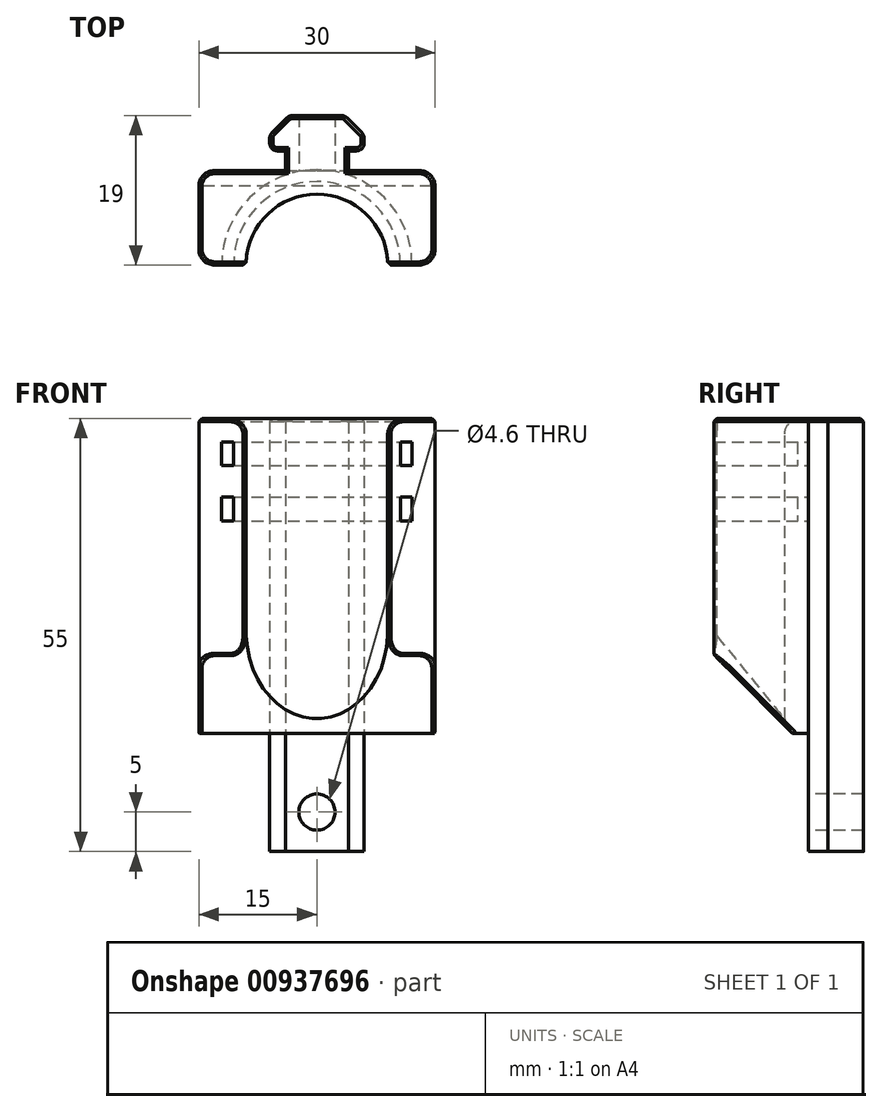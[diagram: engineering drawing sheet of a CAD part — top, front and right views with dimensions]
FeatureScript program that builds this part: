
annotation { "Feature Type Name" : "Feature", "Feature Type Description" : "" }
export const myFeature = defineFeature(function(context is Context, id is Id, definition is map)
    precondition{}
    {
        {
            var Q0;
            Q0=qCreatedBy(makeId("Front.planeOp"),FACE);
            var sketch = newSketch(context, id + "F0", { "sketchPlane" : qUnion([Q0])});
            skLineSegment(sketch, "E0.bottom", {"start": v(-15, 40) * mm, "end": v(15, 40) * mm});
            skLineSegment(sketch, "E0.top", {"start": v(-15, 0) * mm, "end": v(15, 0) * mm});
            skLineSegment(sketch, "E0.left", {"start": v(-15, 40) * mm, "end": v(-15, 0) * mm});
            skLineSegment(sketch, "E0.right", {"start": v(15, 40) * mm, "end": v(15, 0) * mm});
            skSolve(sketch);
        }
        {
            var Q0;
            Q0=makeQuery(id+"F0.imprint","IMPRINT",FACE,{"disambiguationData":[TD([[makeQuery(id+"F0.imprint","IMPRINT",EDGE,{"derivedFrom":sQuery(id+"F0.wireOp",EDGE,"E0.bottom")}),-1.0]])]});
            extrude(context, id + "F1", {"entities" : qUnion([Q0]), "depth" : 3 * mm, "offsetDistance" : 25 * mm});
        }
        {
            var Q0;
            Q0=qCreatedBy(makeId("Top.planeOp"),FACE);
            var sketch = newSketch(context, id + "F2", { "sketchPlane" : qUnion([Q0])});
            skLineSegment(sketch, "E1", {"start": v(-4, 0) * mm, "end": v(-4, 2.5) * mm});
            skLineSegment(sketch, "E2", {"start": v(-4, 2.5) * mm, "end": v(-6, 2.5) * mm});
            skLineSegment(sketch, "E3", {"start": v(-6, 2.5) * mm, "end": v(-6, 4.5) * mm});
            skLineSegment(sketch, "E4", {"start": v(-6, 4.5) * mm, "end": v(-3.5, 7) * mm});
            skLineSegment(sketch, "E5", {"start": v(-3.5, 7) * mm, "end": v(3.5, 7) * mm});
            skLineSegment(sketch, "E6", {"start": v(3.5, 7) * mm, "end": v(6, 4.5) * mm});
            skLineSegment(sketch, "E7", {"start": v(6, 4.5) * mm, "end": v(6, 2.5) * mm});
            skLineSegment(sketch, "E8", {"start": v(6, 2.5) * mm, "end": v(4, 2.5) * mm});
            skLineSegment(sketch, "E9", {"start": v(4, 2.5) * mm, "end": v(4, 0) * mm});
            skLineSegment(sketch, "E10", {"start": v(-4, 0) * mm, "end": v(4, 0) * mm});
            skSolve(sketch);
        }
        {
            var Q0;
            Q0=makeQuery(id+"F2.imprint","IMPRINT",FACE,{"disambiguationData":[TD([[makeQuery(id+"F2.imprint","IMPRINT",EDGE,{"derivedFrom":sQuery(id+"F2.wireOp",EDGE,"E1")}),-1.0]])]});
            var Q1;
            Q1=makeQuery(id+"F1.opExtrude","SWEPT_FACE",FACE,{"disambiguationData":[OSD([sQuery(id+"F0.wireOp",EDGE,"E0.bottom")])]});
            extrude(context, id + "F3", {"entities" : qUnion([Q0]), "operationType" : NewBodyOperationType.ADD, "endBound" : BoundingType.UP_TO_SURFACE, "depth" : 25 * mm, "endBoundEntityFace" : qUnion([Q1]), "offsetDistance" : 25 * mm, "hasSecondDirection" : true, "secondDirectionOppositeDirection" : true, "secondDirectionDepth" : 15 * mm});
        }
        {
            var Q0;
            Q0=makeQuery(id+"F3.boolean.opBoolean","MERGE",FACE,{"derivedFrom":[makeQuery(id+"F1.opExtrude","SWEPT_FACE",FACE,{"disambiguationData":[OSD([sQuery(id+"F0.wireOp",EDGE,"E0.bottom")])]}),makeQuery(id+"F3.opExtrude","CAP_FACE",FACE,{"disambiguationData":[OSD([sQuery(id+"F2.wireOp",EDGE,"E1"),sQuery(id+"F2.wireOp",EDGE,"E2"),sQuery(id+"F2.wireOp",EDGE,"E3"),sQuery(id+"F2.wireOp",EDGE,"E4"),sQuery(id+"F2.wireOp",EDGE,"E5"),sQuery(id+"F2.wireOp",EDGE,"E6"),sQuery(id+"F2.wireOp",EDGE,"E7"),sQuery(id+"F2.wireOp",EDGE,"E8"),sQuery(id+"F2.wireOp",EDGE,"E9"),sQuery(id+"F2.wireOp",EDGE,"E10")])],"isStart":false})]});
            var sketch = newSketch(context, id + "F4", { "sketchPlane" : qUnion([Q0])});
            skCircle(sketch, "E11", {"center": v(0, -12) * mm, "radius": 9 * mm});
            skLineSegment(sketch, "E12", {"start": v(-15, -3) * mm, "end": v(-15, -12) * mm});
            skLineSegment(sketch, "E13", {"start": v(-15, -12) * mm, "end": v(15, -12) * mm});
            skLineSegment(sketch, "E14", {"start": v(15, -12) * mm, "end": v(15, -3) * mm});
            skSolve(sketch);
        }
        {
            var Q0;
            {var subQ6=sQuery(id+"F4.wireOp",EDGE,"E12");Q0=makeQuery(id+"F4.imprint","IMPRINT",FACE,{"disambiguationData":[TD([[makeQuery(id+"F4.imprint","IMPRINT",EDGE,{"derivedFrom":subQ6}),1.0]])]});}
            var Q1;
            {var subQ6=sQuery(id+"F4.wireOp",EDGE,"E14");Q1=makeQuery(id+"F4.imprint","IMPRINT",FACE,{"disambiguationData":[TD([[makeQuery(id+"F4.imprint","IMPRINT",EDGE,{"derivedFrom":subQ6}),1.0]])]});}
            var Q2;
            Q2=makeQuery(id+"F1.opExtrude","SWEPT_FACE",FACE,{"disambiguationData":[OSD([sQuery(id+"F0.wireOp",EDGE,"E0.top")])]});
            extrude(context, id + "F5", {"entities" : qUnion([Q0, Q1]), "operationType" : NewBodyOperationType.ADD, "endBound" : BoundingType.UP_TO_SURFACE, "oppositeDirection" : true, "depth" : 25 * mm, "endBoundEntityFace" : qUnion([Q2]), "offsetDistance" : 25 * mm});
        }
        {
            var Q0;
            {var subQ0=sQuery(id+"F4.wireOp",EDGE,"E13");Q0=makeQuery(id+"F5.opExtrude","CAP_EDGE",EDGE,{"disambiguationData":[OSD([subQ0]),TDD([makeQuery(id+"F4.imprint","IMPRINT",EDGE,{"disambiguationData":[TD([[makeQuery(id+"F4.imprint","INTERSECT",VERTEX,{"derivedFrom":[sQuery(id+"F4.wireOp",EDGE,"E12"),subQ0]}),-1.0]])],"derivedFrom":subQ0})])],"isStart":false});}
            var Q1;
            {var subQ0=sQuery(id+"F4.wireOp",EDGE,"E13");Q1=makeQuery(id+"F5.opExtrude","CAP_EDGE",EDGE,{"disambiguationData":[OSD([subQ0]),TDD([makeQuery(id+"F4.imprint","IMPRINT",EDGE,{"disambiguationData":[TD([[makeQuery(id+"F4.imprint","INTERSECT",VERTEX,{"derivedFrom":[subQ0,sQuery(id+"F4.wireOp",EDGE,"E14")]}),1.0]])],"derivedFrom":subQ0})])],"isStart":false});}
            chamfer(context, id + "F6", {"entities" : qUnion([Q0, Q1]), "chamferType" : ChamferType.OFFSET_ANGLE, "width" : 10 * mm, "oppositeDirection" : false, "angle" : 45 * degree, "tangentPropagation" : true});
        }
        {
            var Q0;
            {var subQ0=sQuery(id+"F4.wireOp",EDGE,"E13");Q0=makeQuery(id+"F5.opExtrude","SWEPT_FACE",FACE,{"disambiguationData":[OSD([subQ0]),TDD([makeQuery(id+"F4.imprint","IMPRINT",EDGE,{"disambiguationData":[TD([[makeQuery(id+"F4.imprint","INTERSECT",VERTEX,{"derivedFrom":[sQuery(id+"F4.wireOp",EDGE,"E12"),subQ0]}),-1.0]])],"derivedFrom":subQ0})])]});}
            var sketch = newSketch(context, id + "F7", { "sketchPlane" : qUnion([Q0])});
            skLineSegment(sketch, "E15.bottom", {"start": v(-12.1, 37) * mm, "end": v(-10.6, 37) * mm});
            skLineSegment(sketch, "E15.top", {"start": v(-12.1, 34) * mm, "end": v(-10.6, 34) * mm});
            skLineSegment(sketch, "E15.left", {"start": v(-12.1, 37) * mm, "end": v(-12.1, 34) * mm});
            skLineSegment(sketch, "E15.right", {"start": v(-10.6, 37) * mm, "end": v(-10.6, 34) * mm});
            skLineSegment(sketch, "E16.bottom", {"start": v(-12.1, 30) * mm, "end": v(-10.6, 30) * mm});
            skLineSegment(sketch, "E16.top", {"start": v(-12.1, 27) * mm, "end": v(-10.6, 27) * mm});
            skLineSegment(sketch, "E16.left", {"start": v(-12.1, 30) * mm, "end": v(-12.1, 27) * mm});
            skLineSegment(sketch, "E16.right", {"start": v(-10.6, 30) * mm, "end": v(-10.6, 27) * mm});
            skLineSegment(sketch, "E17", {"start": v(0, 42) * mm, "end": v(0, 22.6) * mm});
            skSolve(sketch);
        }
        {
            var Q0;
            Q0=makeQuery(id+"F7.imprint","IMPRINT",FACE,{"disambiguationData":[TD([[makeQuery(id+"F7.imprint","IMPRINT",EDGE,{"derivedFrom":sQuery(id+"F7.wireOp",EDGE,"E15.bottom")}),-1.0]])]});
            var Q1;
            Q1=makeQuery(id+"F7.imprint","IMPRINT",FACE,{"disambiguationData":[TD([[makeQuery(id+"F7.imprint","IMPRINT",EDGE,{"derivedFrom":sQuery(id+"F7.wireOp",EDGE,"E16.bottom")}),-1.0]])]});
            var Q2;
            Q2=sQuery(id+"F7.wireOp",EDGE,"E17");
            revolve(context, id + "F8", {"operationType" : NewBodyOperationType.REMOVE, "surfaceOperationType" : NewSurfaceOperationType.NEW, "entities" : qUnion([Q0, Q1]), "axis" : qUnion([Q2]), "revolveType" : RevolveType.FULL, "oppositeDirection" : true});
        }
        {
            var Q0;
            Q0=makeQuery(id+"F3.opExtrude","SWEPT_FACE",FACE,{"disambiguationData":[OSD([sQuery(id+"F2.wireOp",EDGE,"E10")])]});
            var sketch = newSketch(context, id + "F9", { "sketchPlane" : qUnion([Q0])});
            skPoint(sketch, "E18", {"position": v(0, -10) * mm});
            skSolve(sketch);
        }
        {
            var Q0;
            Q0=sQuery(id+"F9.wireOp",VERTEX,"E18");
            var Q1;
            Q1=makeQuery(id+"F1.opExtrude","SWEPT_BODY",BODY,{"disambiguationData":[OSD([sQuery(id+"F0.wireOp",EDGE,"E0.bottom"),sQuery(id+"F0.wireOp",EDGE,"E0.top"),sQuery(id+"F0.wireOp",EDGE,"E0.left"),sQuery(id+"F0.wireOp",EDGE,"E0.right")])]});
            hole(context, id + "F10", {"style" : HoleStyle.SIMPLE, "endStyle" : HoleEndStyle.BLIND, "holeDiameter" : 4.6 * mm, "majorDiameter" : 5 * mm, "holeDepth" : 7 * mm, "isTappedThrough" : true, "tappedDepth" : 20 * mm, "tapClearance" : 3, "locations" : qUnion([Q0]), "scope" : qUnion([Q1])});
        }
        {
            var Q0;
            Q0=makeQuery(id+"F5.opExtrude","SWEPT_EDGE",EDGE,{"disambiguationData":[OSD([sQuery(id+"F4.wireOp",EDGE,"E13"),sQuery(id+"F4.wireOp",EDGE,"E14")])]});
            var Q1;
            Q1=makeQuery(id+"F5.opExtrude","SWEPT_EDGE",EDGE,{"disambiguationData":[OSD([sQuery(id+"F4.wireOp",EDGE,"E12"),sQuery(id+"F4.wireOp",EDGE,"E13")])]});
            var Q2;
            Q2=makeQuery(id+"F1.opExtrude","CAP_EDGE",EDGE,{"disambiguationData":[OSD([sQuery(id+"F0.wireOp",EDGE,"E0.right")])],"isStart":true});
            var Q3;
            Q3=makeQuery(id+"F1.opExtrude","CAP_EDGE",EDGE,{"disambiguationData":[OSD([sQuery(id+"F0.wireOp",EDGE,"E0.left")])],"isStart":true});
            fillet(context, id + "F11", {"entities" : qUnion([Q0, Q1, Q2, Q3]), "radius" : 2 * mm, "tangentPropagation" : true});
        }
        {
            var Q0;
            {var subQ0=sQuery(id+"F4.wireOp",EDGE,"E13");var subQ1=sQuery(id+"F4.wireOp",EDGE,"E11");Q0=makeQuery(id+"F5.boolean.opBoolean","MERGE",EDGE,{"derivedFrom":[makeQuery(id+"F5.opExtrude","CAP_EDGE",EDGE,{"disambiguationData":[OSD([subQ1]),TDD([makeQuery(id+"F4.imprint","IMPRINT",EDGE,{"disambiguationData":[TD([[makeQuery(id+"F4.imprint","INTERSECT",VERTEX,{"disambiguationData":[OD(0.0)],"derivedFrom":[subQ1,subQ0]}),-1.0]])],"derivedFrom":subQ1})])],"isStart":true}),makeQuery(id+"F5.opExtrude","CAP_EDGE",EDGE,{"disambiguationData":[OSD([subQ1]),TDD([makeQuery(id+"F4.imprint","IMPRINT",EDGE,{"disambiguationData":[TD([[makeQuery(id+"F4.imprint","INTERSECT",VERTEX,{"disambiguationData":[OD(1.0)],"derivedFrom":[subQ1,subQ0]}),1.0]])],"derivedFrom":subQ1})])],"isStart":true})]});}
            var Q1;
            {var subQ0=sQuery(id+"F4.wireOp",EDGE,"E13");var subQ1=sQuery(id+"F4.wireOp",EDGE,"E11");var subQ2=makeQuery(id+"F4.imprint","INTERSECT",VERTEX,{"disambiguationData":[OD(1.0)],"derivedFrom":[subQ1,subQ0]});Q1=makeQuery(id+"F6.opChamfer","BLEND_EDGE",EDGE,{"blendedFrom":[makeQuery(id+"F5.opExtrude","CAP_EDGE",EDGE,{"disambiguationData":[OSD([subQ0]),TDD([makeQuery(id+"F4.imprint","IMPRINT",EDGE,{"disambiguationData":[TD([[makeQuery(id+"F4.imprint","INTERSECT",VERTEX,{"derivedFrom":[sQuery(id+"F4.wireOp",EDGE,"E12"),subQ0]}),-1.0]])],"derivedFrom":subQ0})])],"isStart":false}),makeQuery(id+"F5.boolean.opBoolean","MERGE",FACE,{"derivedFrom":[makeQuery(id+"F5.opExtrude","SWEPT_FACE",FACE,{"disambiguationData":[OSD([subQ1]),TDD([makeQuery(id+"F4.imprint","IMPRINT",EDGE,{"disambiguationData":[TD([[makeQuery(id+"F4.imprint","INTERSECT",VERTEX,{"disambiguationData":[OD(0.0)],"derivedFrom":[subQ1,subQ0]}),-1.0]])],"derivedFrom":subQ1})])]}),makeQuery(id+"F5.opExtrude","SWEPT_FACE",FACE,{"disambiguationData":[OSD([subQ1]),TDD([makeQuery(id+"F4.imprint","IMPRINT",EDGE,{"disambiguationData":[TD([[subQ2,1.0]])],"derivedFrom":subQ1})])]})]})],"blendedInto":[makeQuery(id+"F5.boolean.opBoolean","MERGE",FACE,{"derivedFrom":[makeQuery(id+"F5.opExtrude","SWEPT_FACE",FACE,{"disambiguationData":[OSD([subQ1]),TDD([makeQuery(id+"F4.imprint","IMPRINT",EDGE,{"disambiguationData":[TD([[makeQuery(id+"F4.imprint","INTERSECT",VERTEX,{"disambiguationData":[OD(0.0)],"derivedFrom":[subQ1,subQ0]}),-1.0]])],"derivedFrom":subQ1})])]}),makeQuery(id+"F5.opExtrude","SWEPT_FACE",FACE,{"disambiguationData":[OSD([subQ1]),TDD([makeQuery(id+"F4.imprint","IMPRINT",EDGE,{"disambiguationData":[TD([[subQ2,1.0]])],"derivedFrom":subQ1})])]})]})]});}
            fillet(context, id + "F12", {"entities" : qUnion([Q0, Q1]), "radius" : 2 * mm, "tangentPropagation" : true});
        }
        {
            var Q0;
            Q0=makeQuery(id+"F3.opExtrude","SWEPT_EDGE",EDGE,{"disambiguationData":[OSD([sQuery(id+"F2.wireOp",EDGE,"E2"),sQuery(id+"F2.wireOp",EDGE,"E3")])]});
            var Q1;
            Q1=makeQuery(id+"F3.opExtrude","SWEPT_EDGE",EDGE,{"disambiguationData":[OSD([sQuery(id+"F2.wireOp",EDGE,"E3"),sQuery(id+"F2.wireOp",EDGE,"E4")])]});
            var Q2;
            Q2=makeQuery(id+"F3.opExtrude","SWEPT_EDGE",EDGE,{"disambiguationData":[OSD([sQuery(id+"F2.wireOp",EDGE,"E4"),sQuery(id+"F2.wireOp",EDGE,"E5")])]});
            var Q3;
            Q3=makeQuery(id+"F3.opExtrude","SWEPT_EDGE",EDGE,{"disambiguationData":[OSD([sQuery(id+"F2.wireOp",EDGE,"E5"),sQuery(id+"F2.wireOp",EDGE,"E6")])]});
            var Q4;
            Q4=makeQuery(id+"F3.opExtrude","SWEPT_EDGE",EDGE,{"disambiguationData":[OSD([sQuery(id+"F2.wireOp",EDGE,"E6"),sQuery(id+"F2.wireOp",EDGE,"E7")])]});
            var Q5;
            Q5=makeQuery(id+"F3.opExtrude","SWEPT_EDGE",EDGE,{"disambiguationData":[OSD([sQuery(id+"F2.wireOp",EDGE,"E7"),sQuery(id+"F2.wireOp",EDGE,"E8")])]});
            fillet(context, id + "F13", {"entities" : qUnion([Q0, Q1, Q2, Q3, Q4, Q5]), "radius" : 1 * mm, "tangentPropagation" : true});
        }
        {
            var Q0;
            Q0=makeQuery(id+"F5.boolean.opBoolean","MERGE",EDGE,{"derivedFrom":[makeQuery(id+"F1.opExtrude","SWEPT_EDGE",EDGE,{"disambiguationData":[OSD([sQuery(id+"F0.wireOp",EDGE,"E0.bottom"),sQuery(id+"F0.wireOp",EDGE,"E0.left")])]}),makeQuery(id+"F5.opExtrude","CAP_EDGE",EDGE,{"disambiguationData":[OSD([sQuery(id+"F4.wireOp",EDGE,"E12")])],"isStart":true})]});
            var Q1;
            Q1=makeQuery(id+"F3.opExtrude","CAP_EDGE",EDGE,{"disambiguationData":[OSD([sQuery(id+"F2.wireOp",EDGE,"E1")])],"isStart":false});
            var Q2;
            {var subQ0=sQuery(id+"F4.wireOp",EDGE,"E13");var subQ1=sQuery(id+"F4.wireOp",EDGE,"E11");var subQ2=sQuery(id+"F0.wireOp",EDGE,"E0.bottom");var subQ3=sQuery(id+"F2.wireOp",EDGE,"E3");var subQ4=sQuery(id+"F2.wireOp",EDGE,"E2");Q2=makeQuery(id+"F13.opFillet","BLEND_EDGE",EDGE,{"blendedFrom":[makeQuery(id+"F3.opExtrude","SWEPT_EDGE",EDGE,{"disambiguationData":[OSD([subQ4,subQ3])]}),makeQuery(id+"F5.boolean.opBoolean","MERGE",FACE,{"derivedFrom":[makeQuery(id+"F3.boolean.opBoolean","MERGE",FACE,{"derivedFrom":[makeQuery(id+"F1.opExtrude","SWEPT_FACE",FACE,{"disambiguationData":[OSD([subQ2])]}),makeQuery(id+"F3.opExtrude","CAP_FACE",FACE,{"disambiguationData":[OSD([sQuery(id+"F2.wireOp",EDGE,"E1"),subQ4,subQ3,sQuery(id+"F2.wireOp",EDGE,"E4"),sQuery(id+"F2.wireOp",EDGE,"E5"),sQuery(id+"F2.wireOp",EDGE,"E6"),sQuery(id+"F2.wireOp",EDGE,"E7"),sQuery(id+"F2.wireOp",EDGE,"E8"),sQuery(id+"F2.wireOp",EDGE,"E9"),sQuery(id+"F2.wireOp",EDGE,"E10")])],"isStart":false})]}),makeQuery(id+"F5.opExtrude","CAP_FACE",FACE,{"disambiguationData":[OSD([subQ2,subQ1,subQ0,sQuery(id+"F4.wireOp",EDGE,"E14")])],"isStart":true}),makeQuery(id+"F5.opExtrude","CAP_FACE",FACE,{"disambiguationData":[OSD([subQ2,subQ1,sQuery(id+"F4.wireOp",EDGE,"E12"),subQ0])],"isStart":true})]})],"blendedInto":[makeQuery(id+"F5.boolean.opBoolean","MERGE",FACE,{"derivedFrom":[makeQuery(id+"F3.boolean.opBoolean","MERGE",FACE,{"derivedFrom":[makeQuery(id+"F1.opExtrude","SWEPT_FACE",FACE,{"disambiguationData":[OSD([subQ2])]}),makeQuery(id+"F3.opExtrude","CAP_FACE",FACE,{"disambiguationData":[OSD([sQuery(id+"F2.wireOp",EDGE,"E1"),subQ4,subQ3,sQuery(id+"F2.wireOp",EDGE,"E4"),sQuery(id+"F2.wireOp",EDGE,"E5"),sQuery(id+"F2.wireOp",EDGE,"E6"),sQuery(id+"F2.wireOp",EDGE,"E7"),sQuery(id+"F2.wireOp",EDGE,"E8"),sQuery(id+"F2.wireOp",EDGE,"E9"),sQuery(id+"F2.wireOp",EDGE,"E10")])],"isStart":false})]}),makeQuery(id+"F5.opExtrude","CAP_FACE",FACE,{"disambiguationData":[OSD([subQ2,subQ1,subQ0,sQuery(id+"F4.wireOp",EDGE,"E14")])],"isStart":true}),makeQuery(id+"F5.opExtrude","CAP_FACE",FACE,{"disambiguationData":[OSD([subQ2,subQ1,sQuery(id+"F4.wireOp",EDGE,"E12"),subQ0])],"isStart":true})]})]});}
            var Q3;
            Q3=makeQuery(id+"F3.opExtrude","CAP_EDGE",EDGE,{"disambiguationData":[OSD([sQuery(id+"F2.wireOp",EDGE,"E9")])],"isStart":false});
            var Q4;
            {var subQ0=sQuery(id+"F0.wireOp",EDGE,"E0.right");var subQ1=sQuery(id+"F0.wireOp",EDGE,"E0.bottom");Q4=makeQuery(id+"F3.boolean.opBoolean","SPLIT",EDGE,{"disambiguationData":[TD([makeQuery(id+"F1.opExtrude","SWEPT_FACE",FACE,{"disambiguationData":[OSD([subQ0])]})])],"derivedFrom":makeQuery(id+"F1.opExtrude","CAP_EDGE",EDGE,{"disambiguationData":[OSD([subQ1])],"isStart":true})});}
            chamfer(context, id + "F14", {"entities" : qUnion([Q0, Q1, Q2, Q3, Q4]), "width" : .4 * mm, "tangentPropagation" : true});
        }
    });
